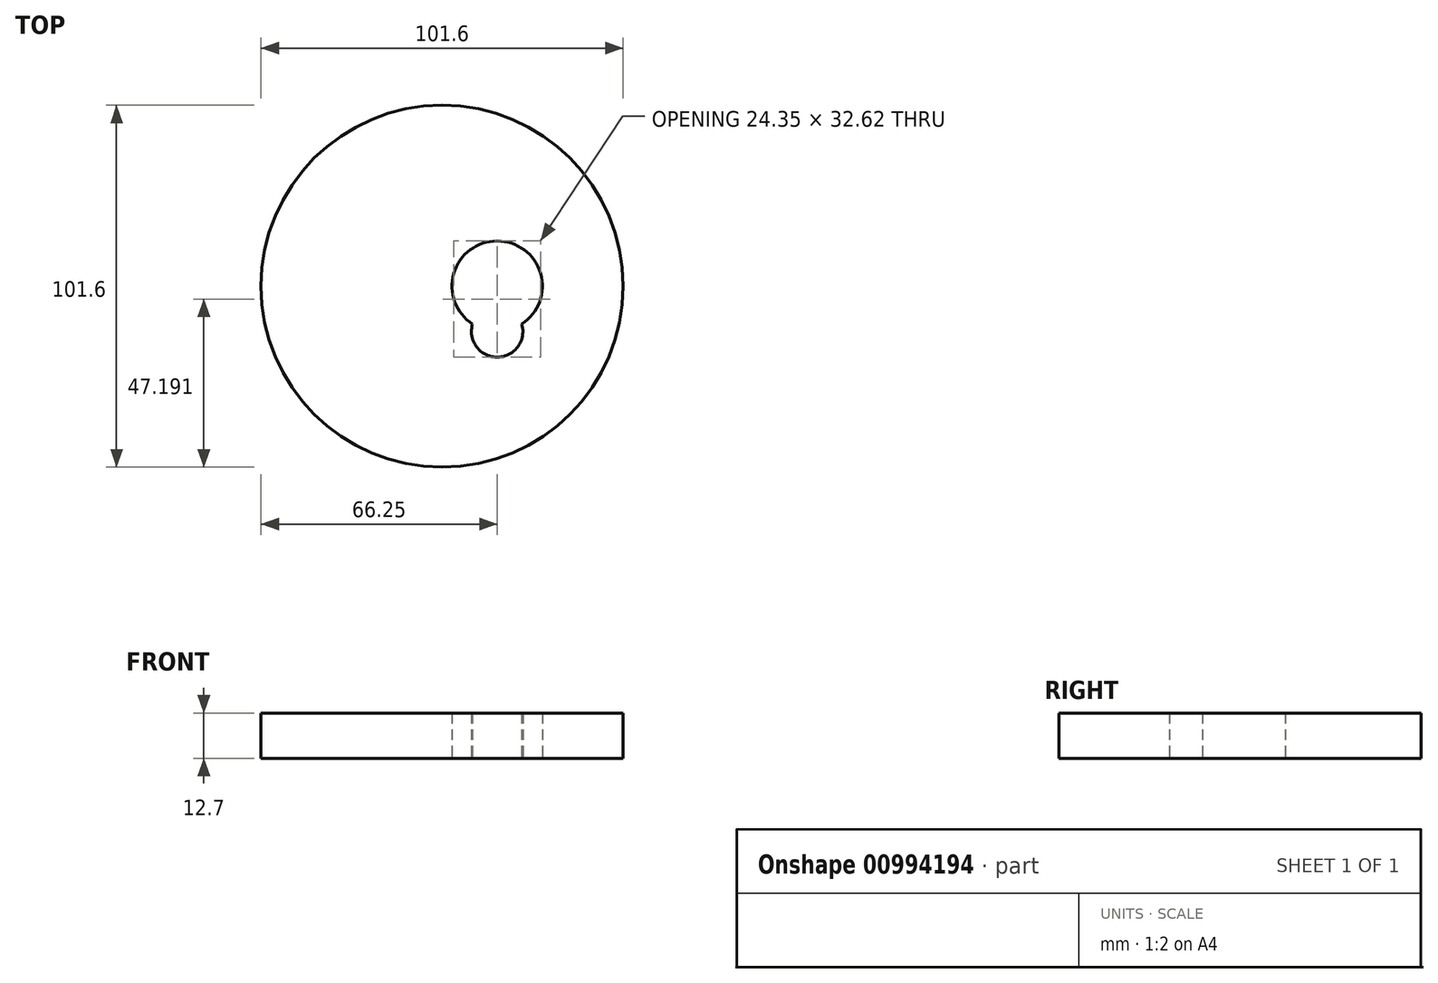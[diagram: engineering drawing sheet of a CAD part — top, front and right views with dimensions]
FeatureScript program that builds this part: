
annotation { "Feature Type Name" : "Feature", "Feature Type Description" : "" }
export const myFeature = defineFeature(function(context is Context, id is Id, definition is map)
    precondition{}
    {
        {
            var Q0;
            Q0=qCreatedBy(makeId("Top.planeOp"),FACE);
            var sketch = newSketch(context, id + "F0", { "sketchPlane" : qUnion([Q0])});
            skCircle(sketch, "E0", {"center": v(-15.45, 0) * mm, "radius": 50.8 * mm});
            skArc(sketch, "E1", {"start": v(6.92, -10.65) * mm, "mid": v(0, 12.7) * mm, "end": v(-6.92, -10.65) * mm});
            skArc(sketch, "E2", {"start": v(-6.92, -10.65) * mm, "mid": v(0, -19.92) * mm, "end": v(6.92, -10.65) * mm});
            skSolve(sketch);
        }
        {
            var Q0;
            Q0=makeQuery(id+"F0.imprint","IMPRINT",FACE,{"disambiguationData":[TD([[makeQuery(id+"F0.imprint","IMPRINT",EDGE,{"derivedFrom":sQuery(id+"F0.wireOp",EDGE,"E0")}),1.0]])]});
            extrude(context, id + "F1", {"entities" : qUnion([Q0]), "depth" : 12.7 * mm, "offsetDistance" : 25.4 * mm});
        }
    });
